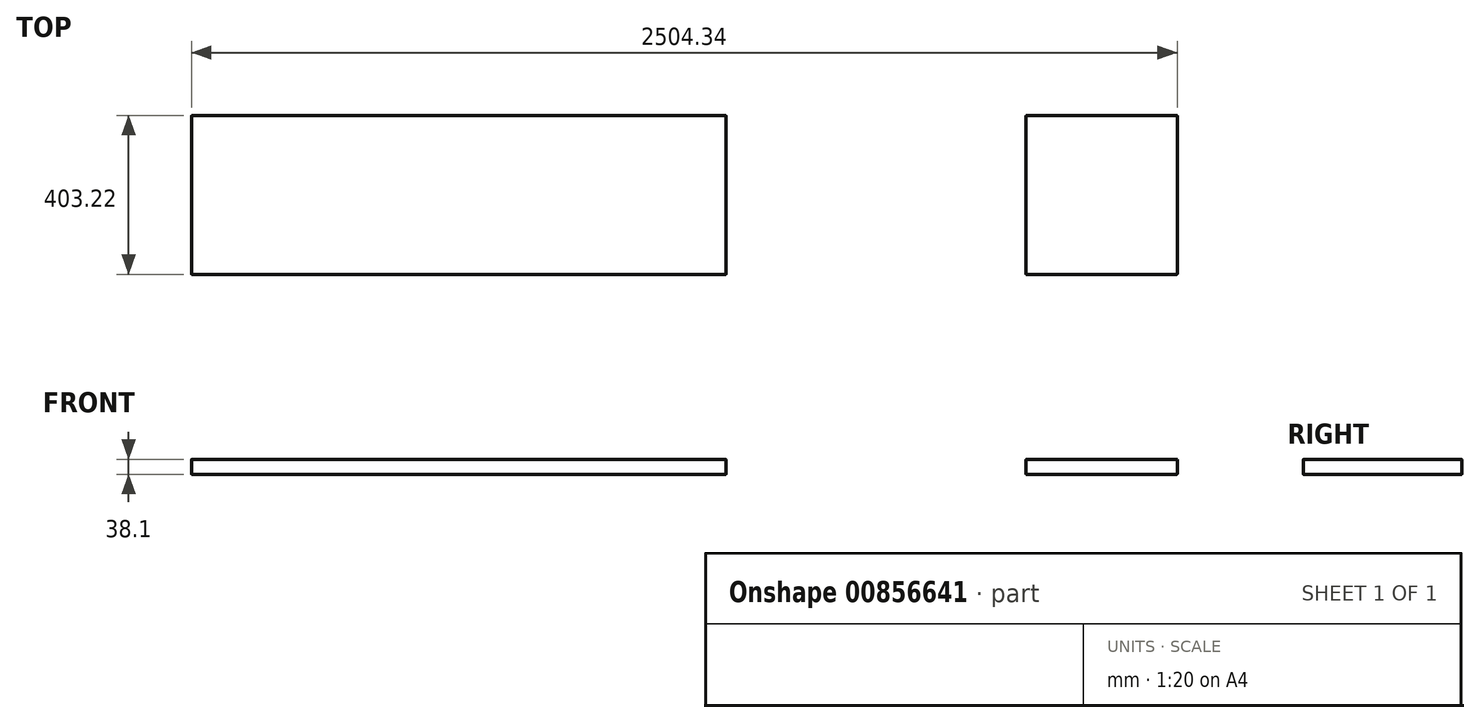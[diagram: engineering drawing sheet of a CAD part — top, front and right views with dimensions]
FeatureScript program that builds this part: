
annotation { "Feature Type Name" : "Feature", "Feature Type Description" : "" }
export const myFeature = defineFeature(function(context is Context, id is Id, definition is map)
    precondition{}
    {
        {
            var Q0;
            Q0=qCreatedBy(makeId("Front.planeOp"),FACE);
            var sketch = newSketch(context, id + "F0", { "sketchPlane" : qUnion([Q0])});
            skLineSegment(sketch, "E0.left", {"start": v(0, 0) * mm, "end": v(0.1, 863.6) * mm});
            skLineSegment(sketch, "E0.right", {"start": v(-1905, -2.15) * mm, "end": v(-1904.9, 861.45) * mm});
            skLineSegment(sketch, "E1.top", {"start": v(0.1, 901.7) * mm, "end": v(-2504.34, 901.7) * mm});
            skLineSegment(sketch, "E1.left", {"start": v(0.1, 863.6) * mm, "end": v(0.1, 901.7) * mm});
            skLineSegment(sketch, "E1.right", {"start": v(-2504.34, 863.6) * mm, "end": v(-2504.34, 901.7) * mm});
            skLineSegment(sketch, "E2", {"start": v(-1904.9, 1058.57) * mm, "end": v(-1904.9, -228.77) * mm, "construction": true});
            skLineSegment(sketch, "E3", {"start": v(0, 1058.57) * mm, "end": v(0, -228.77) * mm, "construction": true});
            skLineSegment(sketch, "E4.bottom", {"start": v(0, 0) * mm, "end": v(-381, 0) * mm});
            skLineSegment(sketch, "E4.left", {"start": v(0, 0) * mm, "end": v(0, 857.25) * mm});
            skLineSegment(sketch, "E5", {"start": v(-381, 0) * mm, "end": v(-387.35, 0) * mm, "construction": true});
            skLineSegment(sketch, "E6.bottom", {"start": v(-387.35, 0) * mm, "end": v(-1143, 0) * mm, "construction": true});
            skLineSegment(sketch, "E6.left", {"start": v(-387.35, 0) * mm, "end": v(-387.35, 736.6) * mm, "construction": true});
            skLineSegment(sketch, "E7", {"start": v(0, 0) * mm, "end": v(-1905, -2.15) * mm, "construction": true});
            skLineSegment(sketch, "E8.bottom", {"start": v(-387.35, 857.25) * mm, "end": v(-1143, 857.25) * mm, "construction": true});
            skLineSegment(sketch, "E8.top", {"start": v(-387.35, 121.5) * mm, "end": v(-1143, 120.65) * mm, "construction": true});
            skLineSegment(sketch, "E8.left", {"start": v(-387.35, 857.25) * mm, "end": v(-387.35, 121.5) * mm, "construction": true});
            skLineSegment(sketch, "E8.right", {"start": v(-1143, 857.25) * mm, "end": v(-1143, 120.65) * mm, "construction": true});
            skLineSegment(sketch, "E9", {"start": v(-1149.35, 857.25) * mm, "end": v(-1149.35, 120.65) * mm, "construction": true});
            skLineSegment(sketch, "E10.bottom", {"start": v(-1149.35, 857.25) * mm, "end": v(-1527.18, 857.25) * mm});
            skLineSegment(sketch, "E10.top", {"start": v(-1149.35, 82.55) * mm, "end": v(-1527.18, 82.55) * mm});
            skLineSegment(sketch, "E10.left", {"start": v(-1149.35, 857.25) * mm, "end": v(-1149.35, 82.55) * mm});
            skLineSegment(sketch, "E10.right", {"start": v(-1527.18, 857.25) * mm, "end": v(-1527.18, 82.55) * mm});
            skLineSegment(sketch, "E11", {"start": v(-1527.18, 82.55) * mm, "end": v(-1533.53, 82.54) * mm, "construction": true});
            skLineSegment(sketch, "E12.bottom", {"start": v(-1533.53, 82.54) * mm, "end": v(-1911.35, 82.54) * mm});
            skLineSegment(sketch, "E12.top", {"start": v(-1533.53, 857.25) * mm, "end": v(-1911.35, 857.25) * mm});
            skLineSegment(sketch, "E12.left", {"start": v(-1533.53, 82.54) * mm, "end": v(-1533.53, 857.25) * mm});
            skLineSegment(sketch, "E12.right", {"start": v(-1911.35, 82.54) * mm, "end": v(-1911.35, 857.25) * mm});
            skLineSegment(sketch, "E13", {"start": v(0, 857.25) * mm, "end": v(-2682.58, 857.25) * mm, "construction": true});
            skLineSegment(sketch, "E14.bottom", {"start": v(0, 857.25) * mm, "end": v(-381, 857.25) * mm});
            skLineSegment(sketch, "E14.top", {"start": v(0, 82.55) * mm, "end": v(-381, 82.55) * mm});
            skLineSegment(sketch, "E14.left", {"start": v(0, 857.25) * mm, "end": v(0, 82.55) * mm});
            skLineSegment(sketch, "E14.right", {"start": v(-381, 857.25) * mm, "end": v(-381, 82.55) * mm});
            skLineSegment(sketch, "E15.bottom", {"start": v(-387.35, 82.55) * mm, "end": v(-1143, 82.55) * mm});
            skLineSegment(sketch, "E15.top", {"start": v(-387.35, 115.22) * mm, "end": v(-1143, 115.22) * mm});
            skLineSegment(sketch, "E15.left", {"start": v(-387.35, 82.55) * mm, "end": v(-387.35, 115.22) * mm});
            skLineSegment(sketch, "E15.right", {"start": v(-1143, 82.55) * mm, "end": v(-1143, 115.22) * mm});
            skPoint(sketch, "E16", {"position": v(-765.18, 121.08) * mm});
            skPoint(sketch, "E17", {"position": v(-1530.35, 82.55) * mm});
            skPoint(sketch, "E17.positionSnap0", {"position": v(-1530.35, 82.55) * mm});
            skLineSegment(sketch, "E18.bottom", {"start": v(0, 0) * mm, "end": v(-3447.41, 0) * mm});
            skLineSegment(sketch, "E18.top", {"start": v(0, 2438.4) * mm, "end": v(-3447.42, 2438.4) * mm});
            skLineSegment(sketch, "E18.right", {"start": v(-3447.41, 0) * mm, "end": v(-3447.42, 2438.4) * mm});
            skLineSegment(sketch, "E19.bottom", {"start": v(-2504.34, 0) * mm, "end": v(-2542.44, 0) * mm});
            skLineSegment(sketch, "E19.top", {"start": v(-2504.34, 2438.4) * mm, "end": v(-2542.44, 2438.4) * mm});
            skLineSegment(sketch, "E19.right", {"start": v(-2542.44, 0) * mm, "end": v(-2542.44, 2438.4) * mm});
            skLineSegment(sketch, "E20", {"start": v(-3447.31, 2438.4) * mm, "end": v(-3447.31, 0) * mm, "construction": true});
            skLineSegment(sketch, "E21.bottom", {"start": v(-3447.31, 2438.4) * mm, "end": v(-3485.52, 2438.4) * mm});
            skLineSegment(sketch, "E21.top", {"start": v(-3447.31, 0) * mm, "end": v(-3485.51, 0) * mm});
            skLineSegment(sketch, "E21.left", {"start": v(-3447.31, 2438.4) * mm, "end": v(-3447.31, 0) * mm});
            skLineSegment(sketch, "E21.right", {"start": v(-3485.52, 2438.4) * mm, "end": v(-3485.51, 0) * mm});
            skLineSegment(sketch, "E22", {"start": v(-3447.31, 1778) * mm, "end": v(-2542.44, 1778) * mm});
            skLineSegment(sketch, "E23", {"start": v(-765.18, 121.08) * mm, "end": v(-765.18, 1778) * mm, "construction": true});
            skPoint(sketch, "E24.middle", {"position": v(-765.18, 1778) * mm});
            skLineSegment(sketch, "E25.top", {"start": v(-2504.34, 1524) * mm, "end": v(-1146.18, 1524) * mm});
            skLineSegment(sketch, "E25.right", {"start": v(-1146.18, 1562.1) * mm, "end": v(-1146.18, 1524) * mm});
            skLineSegment(sketch, "E26.top", {"start": v(-384.18, 1524) * mm, "end": v(0, 1524) * mm});
            skLineSegment(sketch, "E26.left", {"start": v(-384.18, 1562.1) * mm, "end": v(-384.18, 1524) * mm});
            skLineSegment(sketch, "E27.1", {"start": v(-2504.34, 1562.1) * mm, "end": v(-1146.18, 1562.1) * mm});
            skLineSegment(sketch, "E28.0", {"start": v(-384.18, 1562.1) * mm, "end": v(0, 1562.1) * mm});
            skLineSegment(sketch, "E29", {"start": v(-2504.34, 1562.1) * mm, "end": v(-2504.34, 1524) * mm});
            skLineSegment(sketch, "E30", {"start": v(0, 1562.1) * mm, "end": v(0, 1524) * mm});
            skSolve(sketch);
        }
        {
            var Q0;
            Q0=makeQuery(id+"F0.imprint","IMPRINT",FACE,{"disambiguationData":[TD([[makeQuery(id+"F0.imprint","IMPRINT",EDGE,{"derivedFrom":sQuery(id+"F0.wireOp",EDGE,"E25.top")}),1.0]])]});
            var Q1;
            Q1=makeQuery(id+"F0.imprint","IMPRINT",FACE,{"disambiguationData":[TD([[makeQuery(id+"F0.imprint","IMPRINT",EDGE,{"derivedFrom":sQuery(id+"F0.wireOp",EDGE,"E26.top")}),1.0]])]});
            extrude(context, id + "F1", {"entities" : qUnion([Q0, Q1]), "oppositeDirection" : true, "depth" : 609.6 * mm, "offsetDistance" : 25.4 * mm, "hasSecondDirection" : true, "secondDirectionOppositeDirection" : true, "secondDirectionDepth" : 206.38 * mm});
        }
        {
            var Q0;
            Q0=makeQuery(id+"F1.opExtrude","SWEPT_EDGE",EDGE,{"disambiguationData":[OSD([sQuery(id+"F0.wireOp",EDGE,"E25.right"),sQuery(id+"F0.wireOp",EDGE,"E27.1")])]});
            var Q1;
            Q1=makeQuery(id+"F1.opExtrude","CAP_EDGE",EDGE,{"disambiguationData":[OSD([sQuery(id+"F0.wireOp",EDGE,"E27.1")])],"isStart":true});
            var Q2;
            Q2=makeQuery(id+"F1.opExtrude","CAP_EDGE",EDGE,{"disambiguationData":[OSD([sQuery(id+"F0.wireOp",EDGE,"E25.right")])],"isStart":true});
            var Q3;
            Q3=makeQuery(id+"F1.opExtrude","SWEPT_EDGE",EDGE,{"disambiguationData":[OSD([sQuery(id+"F0.wireOp",EDGE,"E25.top"),sQuery(id+"F0.wireOp",EDGE,"E25.right")])]});
            var Q4;
            Q4=makeQuery(id+"F1.opExtrude","CAP_EDGE",EDGE,{"disambiguationData":[OSD([sQuery(id+"F0.wireOp",EDGE,"E25.top")])],"isStart":true});
            var Q5;
            Q5=makeQuery(id+"F1.opExtrude","CAP_EDGE",EDGE,{"disambiguationData":[OSD([sQuery(id+"F0.wireOp",EDGE,"E25.right")])],"isStart":false});
            var Q6;
            Q6=makeQuery(id+"F1.opExtrude","SWEPT_EDGE",EDGE,{"disambiguationData":[OSD([sQuery(id+"F0.wireOp",EDGE,"E27.1"),sQuery(id+"F0.wireOp",EDGE,"E29")])]});
            var Q7;
            Q7=makeQuery(id+"F1.opExtrude","CAP_EDGE",EDGE,{"disambiguationData":[OSD([sQuery(id+"F0.wireOp",EDGE,"E29")])],"isStart":true});
            var Q8;
            Q8=makeQuery(id+"F1.opExtrude","CAP_EDGE",EDGE,{"disambiguationData":[OSD([sQuery(id+"F0.wireOp",EDGE,"E27.1")])],"isStart":false});
            var Q9;
            Q9=makeQuery(id+"F1.opExtrude","CAP_EDGE",EDGE,{"disambiguationData":[OSD([sQuery(id+"F0.wireOp",EDGE,"E28.0")])],"isStart":false});
            var Q10;
            Q10=makeQuery(id+"F1.opExtrude","SWEPT_EDGE",EDGE,{"disambiguationData":[OSD([sQuery(id+"F0.wireOp",EDGE,"E26.left"),sQuery(id+"F0.wireOp",EDGE,"E28.0")])]});
            var Q11;
            Q11=makeQuery(id+"F1.opExtrude","CAP_EDGE",EDGE,{"disambiguationData":[OSD([sQuery(id+"F0.wireOp",EDGE,"E28.0")])],"isStart":true});
            var Q12;
            Q12=makeQuery(id+"F1.opExtrude","CAP_EDGE",EDGE,{"disambiguationData":[OSD([sQuery(id+"F0.wireOp",EDGE,"E26.left")])],"isStart":true});
            var Q13;
            Q13=makeQuery(id+"F1.opExtrude","CAP_EDGE",EDGE,{"disambiguationData":[OSD([sQuery(id+"F0.wireOp",EDGE,"E26.top")])],"isStart":true});
            var Q14;
            Q14=makeQuery(id+"F1.opExtrude","CAP_EDGE",EDGE,{"disambiguationData":[OSD([sQuery(id+"F0.wireOp",EDGE,"E30")])],"isStart":false});
            var Q15;
            Q15=makeQuery(id+"F1.opExtrude","SWEPT_EDGE",EDGE,{"disambiguationData":[OSD([sQuery(id+"F0.wireOp",EDGE,"E26.top"),sQuery(id+"F0.wireOp",EDGE,"E30")])]});
            var Q16;
            Q16=makeQuery(id+"F1.opExtrude","CAP_EDGE",EDGE,{"disambiguationData":[OSD([sQuery(id+"F0.wireOp",EDGE,"E30")])],"isStart":true});
            var Q17;
            Q17=makeQuery(id+"F1.opExtrude","SWEPT_EDGE",EDGE,{"disambiguationData":[OSD([sQuery(id+"F0.wireOp",EDGE,"E28.0"),sQuery(id+"F0.wireOp",EDGE,"E30")])]});
            var Q18;
            Q18=makeQuery(id+"F1.opExtrude","CAP_EDGE",EDGE,{"disambiguationData":[OSD([sQuery(id+"F0.wireOp",EDGE,"E26.left")])],"isStart":false});
            var Q19;
            Q19=makeQuery(id+"F1.opExtrude","CAP_EDGE",EDGE,{"disambiguationData":[OSD([sQuery(id+"F0.wireOp",EDGE,"E26.top")])],"isStart":false});
            var Q20;
            Q20=makeQuery(id+"F1.opExtrude","SWEPT_EDGE",EDGE,{"disambiguationData":[OSD([sQuery(id+"F0.wireOp",EDGE,"E25.top"),sQuery(id+"F0.wireOp",EDGE,"E29")])]});
            var Q21;
            Q21=makeQuery(id+"F1.opExtrude","CAP_EDGE",EDGE,{"disambiguationData":[OSD([sQuery(id+"F0.wireOp",EDGE,"E25.top")])],"isStart":false});
            var Q22;
            Q22=makeQuery(id+"F1.opExtrude","CAP_EDGE",EDGE,{"disambiguationData":[OSD([sQuery(id+"F0.wireOp",EDGE,"E29")])],"isStart":false});
            fillet(context, id + "F2", {"entities" : qUnion([Q0, Q1, Q2, Q3, Q4, Q5, Q6, Q7, Q8, Q9, Q10, Q11, Q12, Q13, Q14, Q15, Q16, Q17, Q18, Q19, Q20, Q21, Q22]), "radius" : 0.76 * mm, "tangentPropagation" : true, "allowEdgeOverflow" : false});
        }
    });
